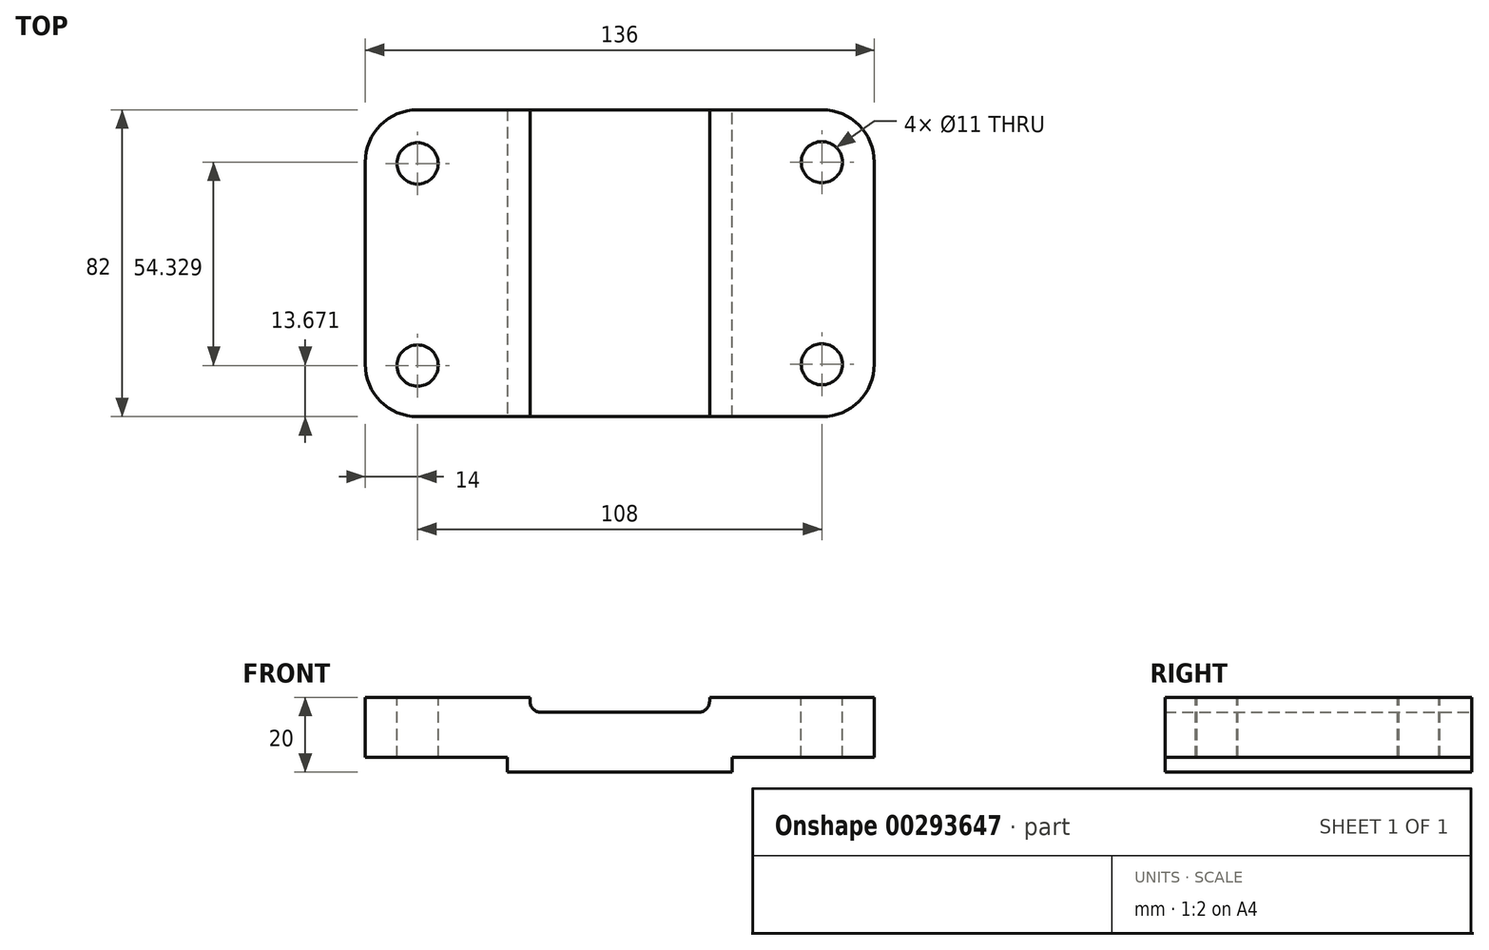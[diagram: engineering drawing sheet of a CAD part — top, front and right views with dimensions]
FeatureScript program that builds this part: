
annotation { "Feature Type Name" : "Feature", "Feature Type Description" : "" }
export const myFeature = defineFeature(function(context is Context, id is Id, definition is map)
    precondition{}
    {
        {
            var Q0;
            Q0=qCreatedBy(makeId("Top.planeOp"),FACE);
            var sketch = newSketch(context, id + "F0", { "sketchPlane" : qUnion([Q0])});
            skLineSegment(sketch, "E0", {"start": v(-68, -14) * mm, "end": v(-68, -68) * mm});
            skLineSegment(sketch, "E1", {"start": v(-54, 0) * mm, "end": v(54, 0) * mm});
            skLineSegment(sketch, "E2", {"start": v(68, -14) * mm, "end": v(68, -68) * mm});
            skLineSegment(sketch, "E3", {"start": v(-54, -82) * mm, "end": v(54, -82) * mm});
            skArc(sketch, "E4", {"start": v(-54, 0) * mm, "mid": v(-63.9, -4.1) * mm, "end": v(-68, -14) * mm});
            skArc(sketch, "E5", {"start": v(-68, -68) * mm, "mid": v(-63.9, -77.9) * mm, "end": v(-54, -82) * mm});
            skArc(sketch, "E6", {"start": v(54, -82) * mm, "mid": v(63.9, -77.9) * mm, "end": v(68, -68) * mm});
            skArc(sketch, "E7", {"start": v(68, -14) * mm, "mid": v(63.9, -4.1) * mm, "end": v(54, 0) * mm});
            skSolve(sketch);
        }
        {
            var Q0;
            Q0 = qSketchRegion(id + "F0", true);
            extrude(context, id + "F1", {"entities" : qUnion([Q0]), "depth" : 16 * mm});
        }
        {
            var Q0;
            Q0=qCreatedBy(makeId("Top.planeOp"),FACE);
            var sketch = newSketch(context, id + "F2", { "sketchPlane" : qUnion([Q0])});
            skLineSegment(sketch, "E8", {"start": v(-30, 0) * mm, "end": v(-30, -82) * mm});
            skLineSegment(sketch, "E9", {"start": v(-30, -82) * mm, "end": v(30, -82) * mm});
            skLineSegment(sketch, "E10", {"start": v(30, -82) * mm, "end": v(30, 0) * mm});
            skLineSegment(sketch, "E11", {"start": v(30, 0) * mm, "end": v(-30, 0) * mm});
            skSolve(sketch);
        }
        {
            var Q0;
            Q0 = qSketchRegion(id + "F2", true);
            extrude(context, id + "F3", {"entities" : qUnion([Q0]), "operationType" : NewBodyOperationType.ADD, "oppositeDirection" : true, "depth" : 4 * mm});
        }
        {
            var Q0;
            Q0=makeQuery(id+"F1.opExtrude","CAP_FACE",FACE,{"disambiguationData":[OSD([sQuery(id+"F0.wireOp",EDGE,"E0"),sQuery(id+"F0.wireOp",EDGE,"E1"),sQuery(id+"F0.wireOp",EDGE,"E2"),sQuery(id+"F0.wireOp",EDGE,"E3"),sQuery(id+"F0.wireOp",EDGE,"E4"),sQuery(id+"F0.wireOp",EDGE,"E5"),sQuery(id+"F0.wireOp",EDGE,"E6"),sQuery(id+"F0.wireOp",EDGE,"E7")])],"isStart":false});
            var sketch = newSketch(context, id + "F4", { "sketchPlane" : qUnion([Q0])});
            skLineSegment(sketch, "E12", {"start": v(-24, 0) * mm, "end": v(-24, -82) * mm});
            skLineSegment(sketch, "E13", {"start": v(-24, -82) * mm, "end": v(24, -82) * mm});
            skLineSegment(sketch, "E14", {"start": v(24, -82) * mm, "end": v(24, 0) * mm});
            skLineSegment(sketch, "E15", {"start": v(24, 0) * mm, "end": v(-24, 0) * mm});
            skSolve(sketch);
        }
        {
            var Q0;
            Q0 = qSketchRegion(id + "F4", true);
            extrude(context, id + "F5", {"entities" : qUnion([Q0]), "operationType" : NewBodyOperationType.REMOVE, "oppositeDirection" : true, "depth" : 4 * mm});
        }
        {
            var Q0;
            Q0=makeQuery(id+"F5.boolean.opBoolean","COPY",EDGE,{"derivedFrom":makeQuery(id+"F5.opExtrude","CAP_EDGE",EDGE,{"disambiguationData":[OSD([sQuery(id+"F4.wireOp",EDGE,"E12")])],"isStart":false})});
            var Q1;
            Q1=makeQuery(id+"F5.boolean.opBoolean","COPY",EDGE,{"derivedFrom":makeQuery(id+"F5.opExtrude","CAP_EDGE",EDGE,{"disambiguationData":[OSD([sQuery(id+"F4.wireOp",EDGE,"E14")])],"isStart":false})});
            fillet(context, id + "F6", {"entities" : qUnion([Q0, Q1]), "radius" : 3 * mm, "tangentPropagation" : true, "allowEdgeOverflow" : false});
        }
        {
            var Q0;
            {var subQ0=sQuery(id+"F0.wireOp",EDGE,"E3");var subQ1=sQuery(id+"F0.wireOp",EDGE,"E2");var subQ2=sQuery(id+"F0.wireOp",EDGE,"E6");var subQ3=sQuery(id+"F0.wireOp",EDGE,"E1");var subQ4=sQuery(id+"F0.wireOp",EDGE,"E7");Q0=makeQuery(id+"F5.boolean.opBoolean","SPLIT",FACE,{"disambiguationData":[TD([makeQuery(id+"F1.opExtrude","SWEPT_FACE",FACE,{"disambiguationData":[OSD([subQ1])]})])],"derivedFrom":makeQuery(id+"F1.opExtrude","CAP_FACE",FACE,{"disambiguationData":[OSD([sQuery(id+"F0.wireOp",EDGE,"E0"),subQ3,subQ1,subQ0,sQuery(id+"F0.wireOp",EDGE,"E4"),sQuery(id+"F0.wireOp",EDGE,"E5"),subQ2,subQ4])],"isStart":false})});}
            var sketch = newSketch(context, id + "F7", { "sketchPlane" : qUnion([Q0])});
            skCircle(sketch, "E16", {"center": v(54, -14) * mm, "radius": 5.5 * mm});
            skCircle(sketch, "E17", {"center": v(54, -68) * mm, "radius": 5.5 * mm});
            skCircle(sketch, "E18", {"center": v(-54, -14.33) * mm, "radius": 5.5 * mm});
            skCircle(sketch, "E19", {"center": v(-54, -68.33) * mm, "radius": 5.5 * mm});
            skSolve(sketch);
        }
        {
            var Q0;
            Q0 = qSketchRegion(id + "F7", true);
            extrude(context, id + "F8", {"entities" : qUnion([Q0]), "operationType" : NewBodyOperationType.REMOVE, "endBound" : BoundingType.THROUGH_ALL, "oppositeDirection" : true, "depth" : 25 * mm});
        }
    });
